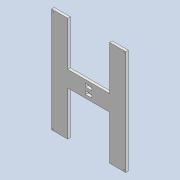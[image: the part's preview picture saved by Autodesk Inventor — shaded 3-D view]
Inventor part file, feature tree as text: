
AUTODESK INVENTOR PART (.ipt)
format: ipt  version: 2020 (Build 240168000, 168)  size: 139,264 bytes
history: native  units: mm
features: sketch x4, extrude x3, hole x1
ambient origin geometry x8: Origin, YZ Plane, XZ Plane, XY Plane, X Axis, Y Axis, Z Axis, Center Point
bodies: Solid1 (feature_tree)
feature tree (8):
  extrude  "Extrusion1"  Depth=325.0mm
  hole  "Hole1"  [1 undecoded]
  extrude  "Extrusion2"  Depth=50.0mm
  extrude  "Extrusion3"  Depth=50.0mm
  sketch  "Sketch1"  dims[d0=230.0mm d1=325.0mm]
  sketch  "Sketch2"  dims[d2=8.0mm d3=0.0mm d4=5.0mm]
  sketch  "Sketch3"  dims[d5=5.0mm]
  sketch  "Sketch4"  dims[d6=3.5mm d7=6.0mm d8=4.0mm d9=2.0mm d10=90.0deg d11=21.0mm d12=0.0mm d13=50.0mm d14=50.0mm d15=25.0mm d16=25.0mm d17=10.0mm d18=0.0mm d19=10.0mm d20=10.0mm d21=10.0mm d22=20.0mm d23=0.0mm d24=0.0mm]
note: 1 required parameter value undecoded (feature->parameter linkage not recoverable at this tier; creation-order binding heuristic only, values carry confidence <= 0.55)
